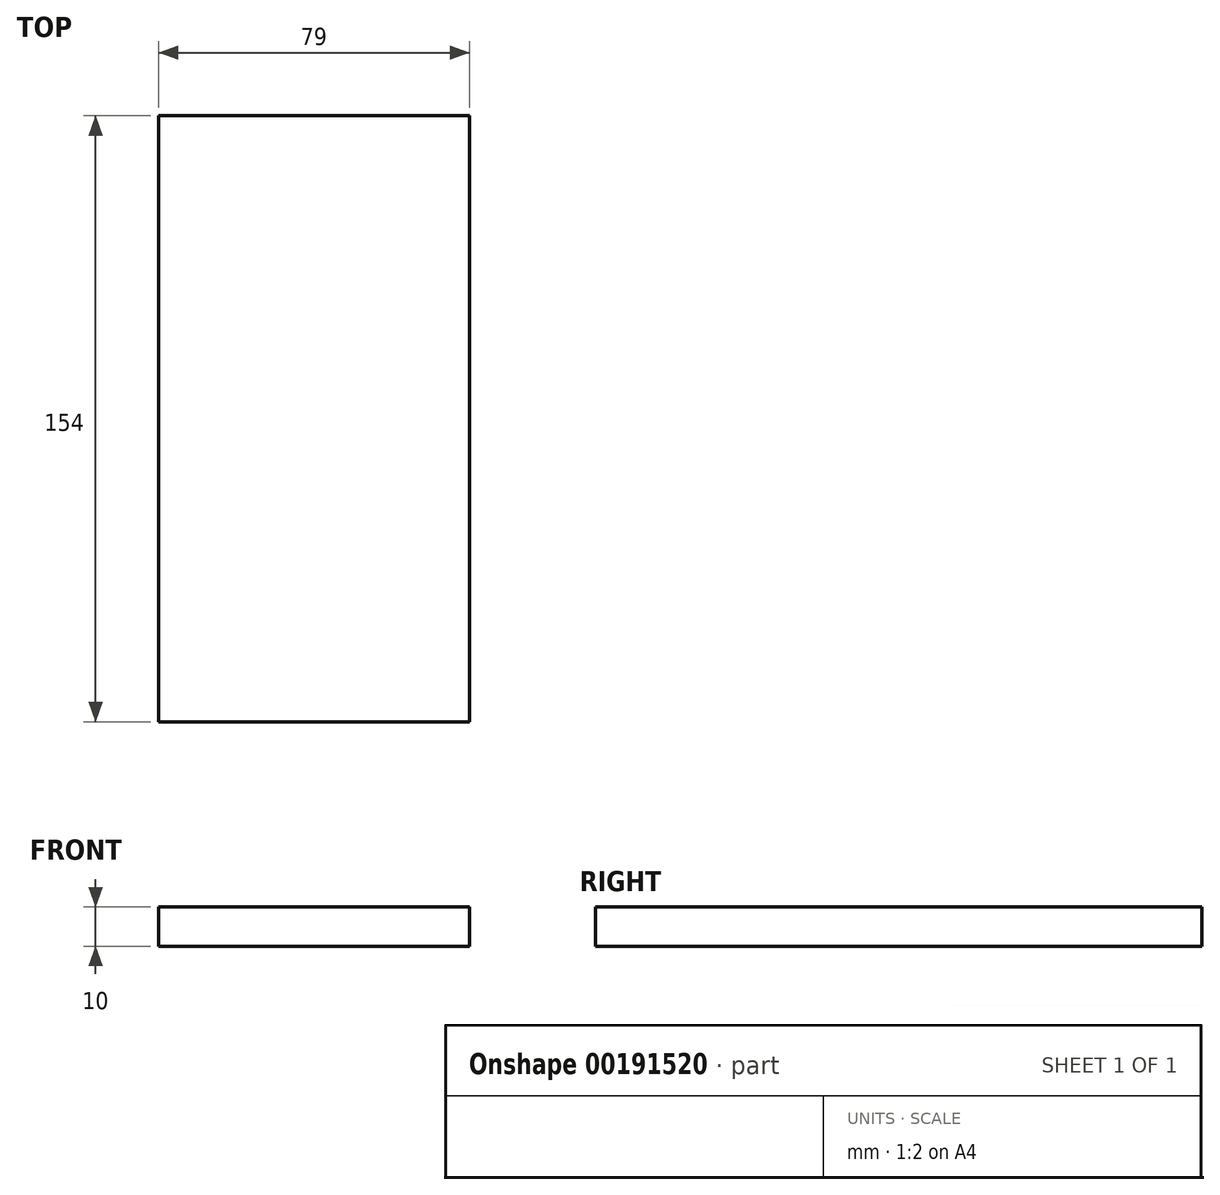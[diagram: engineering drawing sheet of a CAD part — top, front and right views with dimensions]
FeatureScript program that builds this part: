
annotation { "Feature Type Name" : "Feature", "Feature Type Description" : "" }
export const myFeature = defineFeature(function(context is Context, id is Id, definition is map)
    precondition{}
    {
        {
            var Q0;
            Q0=qCreatedBy(makeId("Top.planeOp"),FACE);
            var sketch = newSketch(context, id + "F0", { "sketchPlane" : qUnion([Q0])});
            skLineSegment(sketch, "E0.bottom", {"start": v(-39.5, 77) * mm, "end": v(39.5, 77) * mm});
            skLineSegment(sketch, "E0.top", {"start": v(-39.5, -77) * mm, "end": v(39.5, -77) * mm});
            skLineSegment(sketch, "E0.left", {"start": v(-39.5, 77) * mm, "end": v(-39.5, -77) * mm});
            skLineSegment(sketch, "E0.right", {"start": v(39.5, 77) * mm, "end": v(39.5, -77) * mm});
            skPoint(sketch, "E0.middle", {"position": v(0, 0) * mm});
            skSolve(sketch);
        }
        {
            var Q0;
            Q0=makeQuery(id+"F0.imprint","IMPRINT",FACE,{"disambiguationData":[TD([[makeQuery(id+"F0.imprint","IMPRINT",EDGE,{"derivedFrom":sQuery(id+"F0.wireOp",EDGE,"E0.bottom")}),-1.0]])]});
            extrude(context, id + "F1", {"entities" : qUnion([Q0]), "oppositeDirection" : true, "depth" : 10 * mm});
        }
    });
